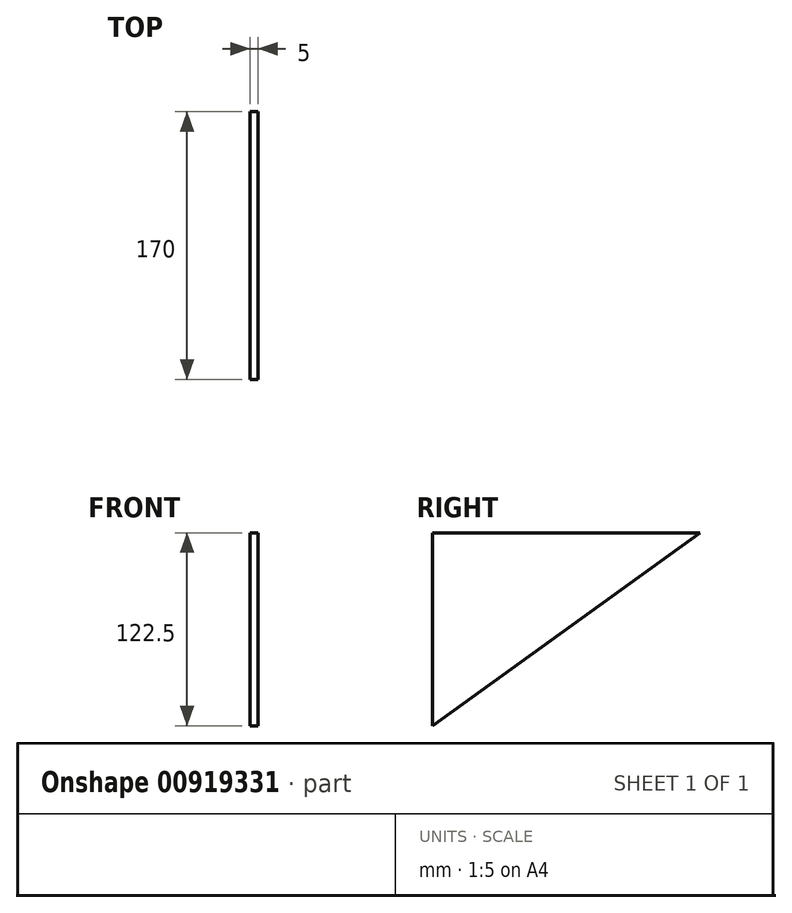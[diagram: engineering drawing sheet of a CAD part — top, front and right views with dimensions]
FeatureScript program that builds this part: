
annotation { "Feature Type Name" : "Feature", "Feature Type Description" : "" }
export const myFeature = defineFeature(function(context is Context, id is Id, definition is map)
    precondition{}
    {
        {
            var Q0;
            Q0=qCreatedBy(makeId("Right.planeOp"),FACE);
            var sketch = newSketch(context, id + "F0", { "sketchPlane" : qUnion([Q0])});
            skLineSegment(sketch, "E0", {"start": v(0, 0) * mm, "end": v(0, 122.5) * mm});
            skLineSegment(sketch, "E1", {"start": v(0, 122.5) * mm, "end": v(170, 122.5) * mm});
            skLineSegment(sketch, "E2", {"start": v(170, 122.5) * mm, "end": v(0, 0) * mm});
            skSolve(sketch);
        }
        {
            var Q0;
            Q0=makeQuery(id+"F0.imprint","IMPRINT",FACE,{"disambiguationData":[TD([[makeQuery(id+"F0.imprint","IMPRINT",EDGE,{"derivedFrom":sQuery(id+"F0.wireOp",EDGE,"E0")}),-1.0]])]});
            extrude(context, id + "F1", {"entities" : qUnion([Q0]), "depth" : 5 * mm, "offsetDistance" : 25 * mm});
        }
    });
